# Revit family: Sink-Wall_Mount-KOHLER-Chesapeake-K-1722
name_source: partatom
category: Plumbing Fixtures
revit_build: Autodesk Revit 2015 (Build: 20140606_1530(x64)
units: mm (PartAtom-declared; Revit-internal decimal feet)

## types (3) — shared parameters
ADA Compliant = Yes
Assembly Code = D2010400
CW Connection = No
Cold Water Inlet = Cold Water Inlet
Date Modified = 08/28/2018
Default Elevation = 34"
Description = 19-1/4inch x 17-1/4inch wall-mount/concealed arm carrier bathroom sink with single faucet hole
Drain Included = No
Environmental Product Declaration = https://www.us.kohler.com
HW Connection = No
Height = 10 3/8"
Hot Water Inlet = Hot Water Inlet
Length = 19 1/4"
Manufacturer = KOHLER Co.
MasterFormat 1995 = 15410
MasterFormat 2004 = 22.41.16
Material = Vitreous china
Product Documentation Link = http://www.us.kohler.com
Product Name = Chesapeake
Product Page URL = http://www.us.kohler.com
URL = https://www.us.kohler.com
Vent Connection = No
Waste Connection = Yes
Waste Water Outlet = Waste Water Outlet
Width = 17 1/4"

## per-type parameters (varying)
| type | Finish | Model | Type |
| 0-White | Kohler-Vitreous_China-0-White | K-1722-0 | 1 |
| 96-Biscuit | Kohler-Vitreous_China-96-Biscuit | K-1722-96 | 2 |
| 47-Almond | Kohler-Vitreous_China-47-Almond | K-1722-47 | 3 |

## geometry (parser evidence)
native form markers: Sweep x5
no freeform markers — native parametric forms only
